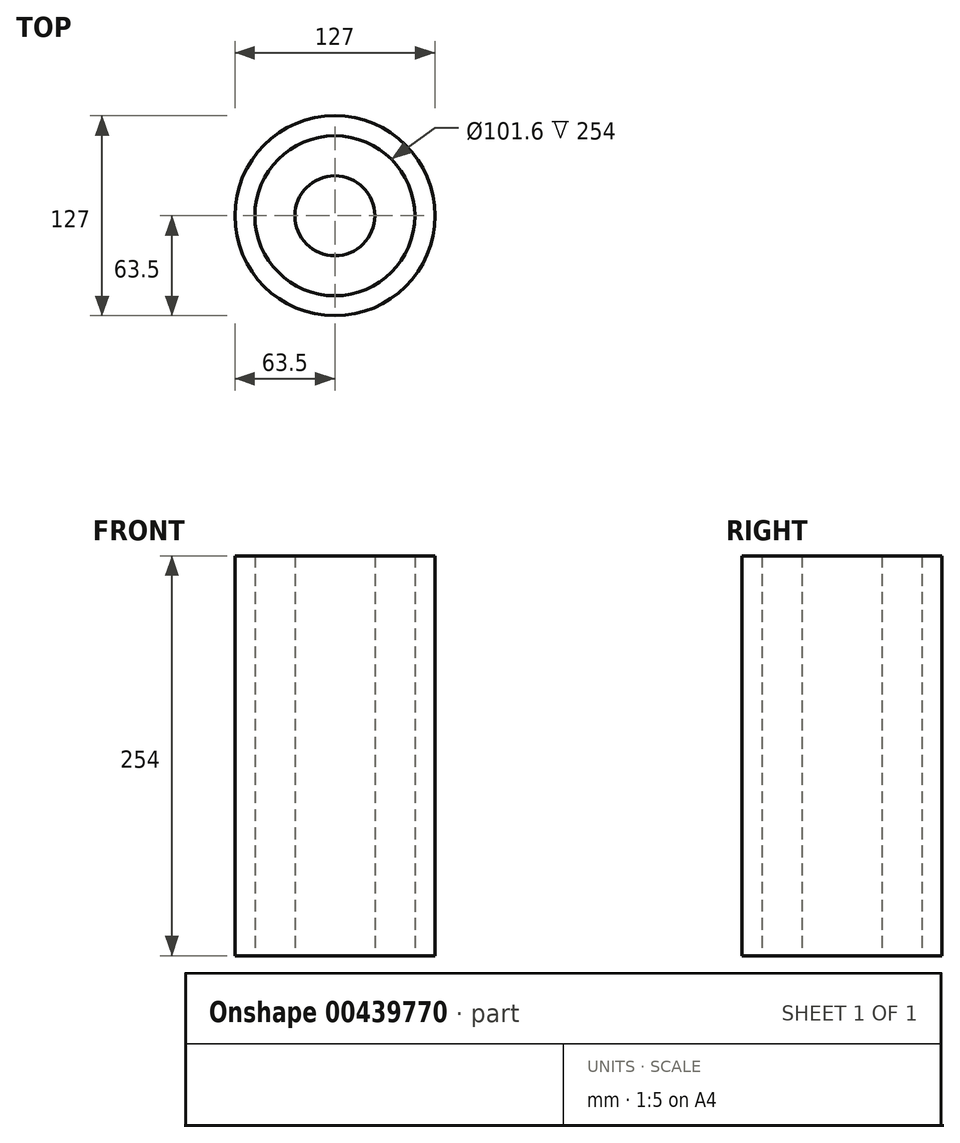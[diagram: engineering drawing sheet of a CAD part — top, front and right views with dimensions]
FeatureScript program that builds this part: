
annotation { "Feature Type Name" : "Feature", "Feature Type Description" : "" }
export const myFeature = defineFeature(function(context is Context, id is Id, definition is map)
    precondition{}
    {
        {
            var Q0;
            Q0=qCreatedBy(makeId("Top.planeOp"),FACE);
            var sketch = newSketch(context, id + "F0", { "sketchPlane" : qUnion([Q0])});
            skCircle(sketch, "E0", {"center": v(0, 0) * mm, "radius": 63.5 * mm});
            skCircle(sketch, "E1", {"center": v(0, 0) * mm, "radius": 50.8 * mm});
            skCircle(sketch, "E2", {"center": v(0, 0) * mm, "radius": 25.4 * mm});
            skSolve(sketch);
        }
        {
            var Q0;
            Q0=makeQuery(id+"F0.imprint","IMPRINT",FACE,{"disambiguationData":[TD([[makeQuery(id+"F0.imprint","IMPRINT",EDGE,{"derivedFrom":sQuery(id+"F0.wireOp",EDGE,"E2")}),1.0]])]});
            var Q1;
            Q1=makeQuery(id+"F0.imprint","IMPRINT",FACE,{"disambiguationData":[TD([[makeQuery(id+"F0.imprint","IMPRINT",EDGE,{"derivedFrom":sQuery(id+"F0.wireOp",EDGE,"E0")}),1.0]])]});
            extrude(context, id + "F1", {"entities" : qUnion([Q0, Q1]), "endBound" : BoundingType.SYMMETRIC, "depth" : 254 * mm});
        }
    });
